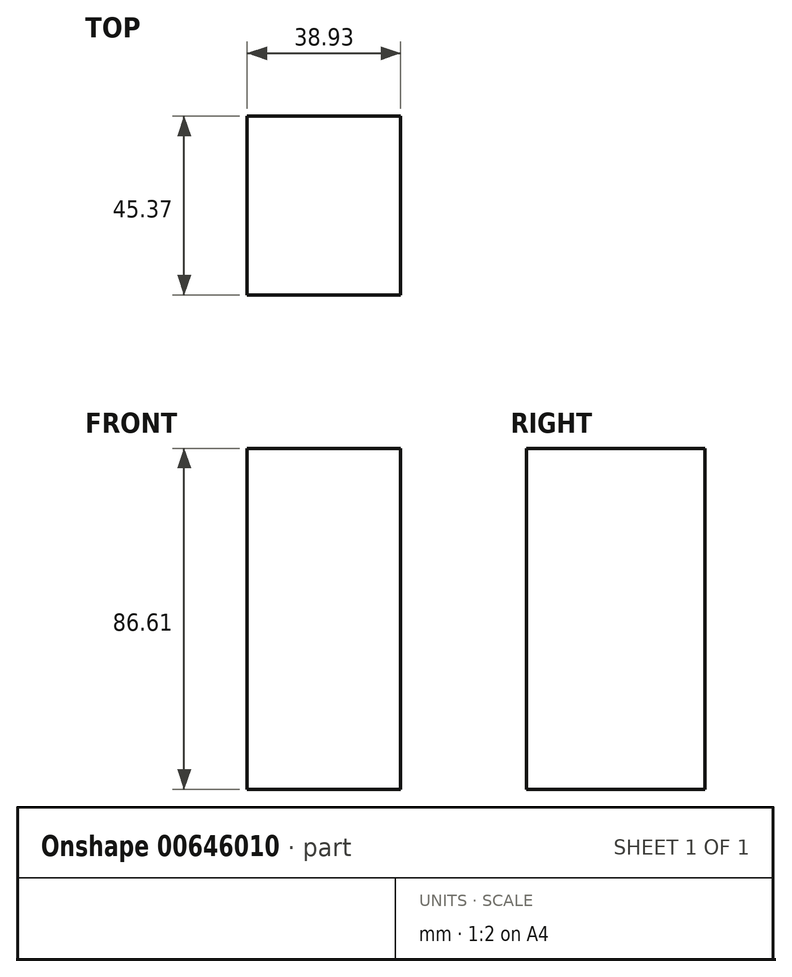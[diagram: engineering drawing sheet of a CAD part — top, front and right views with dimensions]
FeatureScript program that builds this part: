
annotation { "Feature Type Name" : "Feature", "Feature Type Description" : "" }
export const myFeature = defineFeature(function(context is Context, id is Id, definition is map)
    precondition{}
    {
        {
            var Q0;
            Q0=qCreatedBy(makeId("Top.planeOp"),FACE);
            var sketch = newSketch(context, id + "F0", { "sketchPlane" : qUnion([Q0])});
            skLineSegment(sketch, "E0", {"start": v(0, 0) * mm, "end": v(0, 45.37) * mm});
            skLineSegment(sketch, "E1", {"start": v(0, 45.37) * mm, "end": v(38.93, 45.37) * mm});
            skLineSegment(sketch, "E2", {"start": v(38.93, 45.37) * mm, "end": v(38.93, 0) * mm});
            skLineSegment(sketch, "E3", {"start": v(38.93, 0) * mm, "end": v(0, 0) * mm});
            skSolve(sketch);
        }
        {
            var Q0;
            Q0=makeQuery(id+"F0.imprint","IMPRINT",FACE,{"disambiguationData":[TD([[makeQuery(id+"F0.imprint","IMPRINT",EDGE,{"derivedFrom":sQuery(id+"F0.wireOp",EDGE,"E0")}),-1.0]])]});
            extrude(context, id + "F1", {"entities" : qUnion([Q0]), "oppositeDirection" : true, "depth" : 86.61 * mm, "offsetDistance" : 25.4 * mm});
        }
    });
